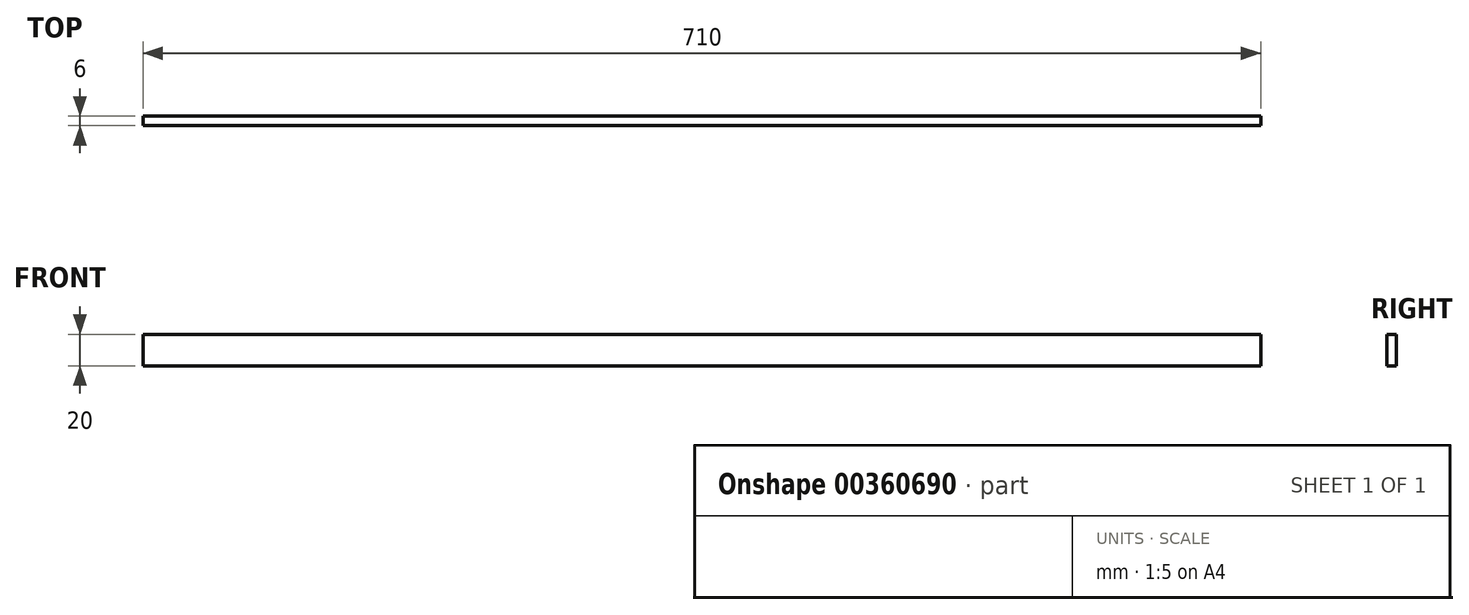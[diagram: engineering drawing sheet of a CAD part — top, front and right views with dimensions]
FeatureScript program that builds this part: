
annotation { "Feature Type Name" : "Feature", "Feature Type Description" : "" }
export const myFeature = defineFeature(function(context is Context, id is Id, definition is map)
    precondition{}
    {
        {
            var Q0;
            Q0=qCreatedBy(makeId("Front.planeOp"),FACE);
            var sketch = newSketch(context, id + "F0", { "sketchPlane" : qUnion([Q0])});
            skLineSegment(sketch, "E0.bottom", {"start": v(0, 0) * mm, "end": v(710, 0) * mm});
            skLineSegment(sketch, "E0.top", {"start": v(0, 20) * mm, "end": v(710, 20) * mm});
            skLineSegment(sketch, "E0.left", {"start": v(0, 0) * mm, "end": v(0, 20) * mm});
            skLineSegment(sketch, "E0.right", {"start": v(710, 0) * mm, "end": v(710, 20) * mm});
            skSolve(sketch);
        }
        {
            var Q0;
            Q0=makeQuery(id+"F0.imprint","IMPRINT",FACE,{"disambiguationData":[TD([[makeQuery(id+"F0.imprint","IMPRINT",EDGE,{"derivedFrom":sQuery(id+"F0.wireOp",EDGE,"E0.bottom")}),1.0]])]});
            extrude(context, id + "F1", {"entities" : qUnion([Q0]), "depth" : 6 * mm});
        }
    });
